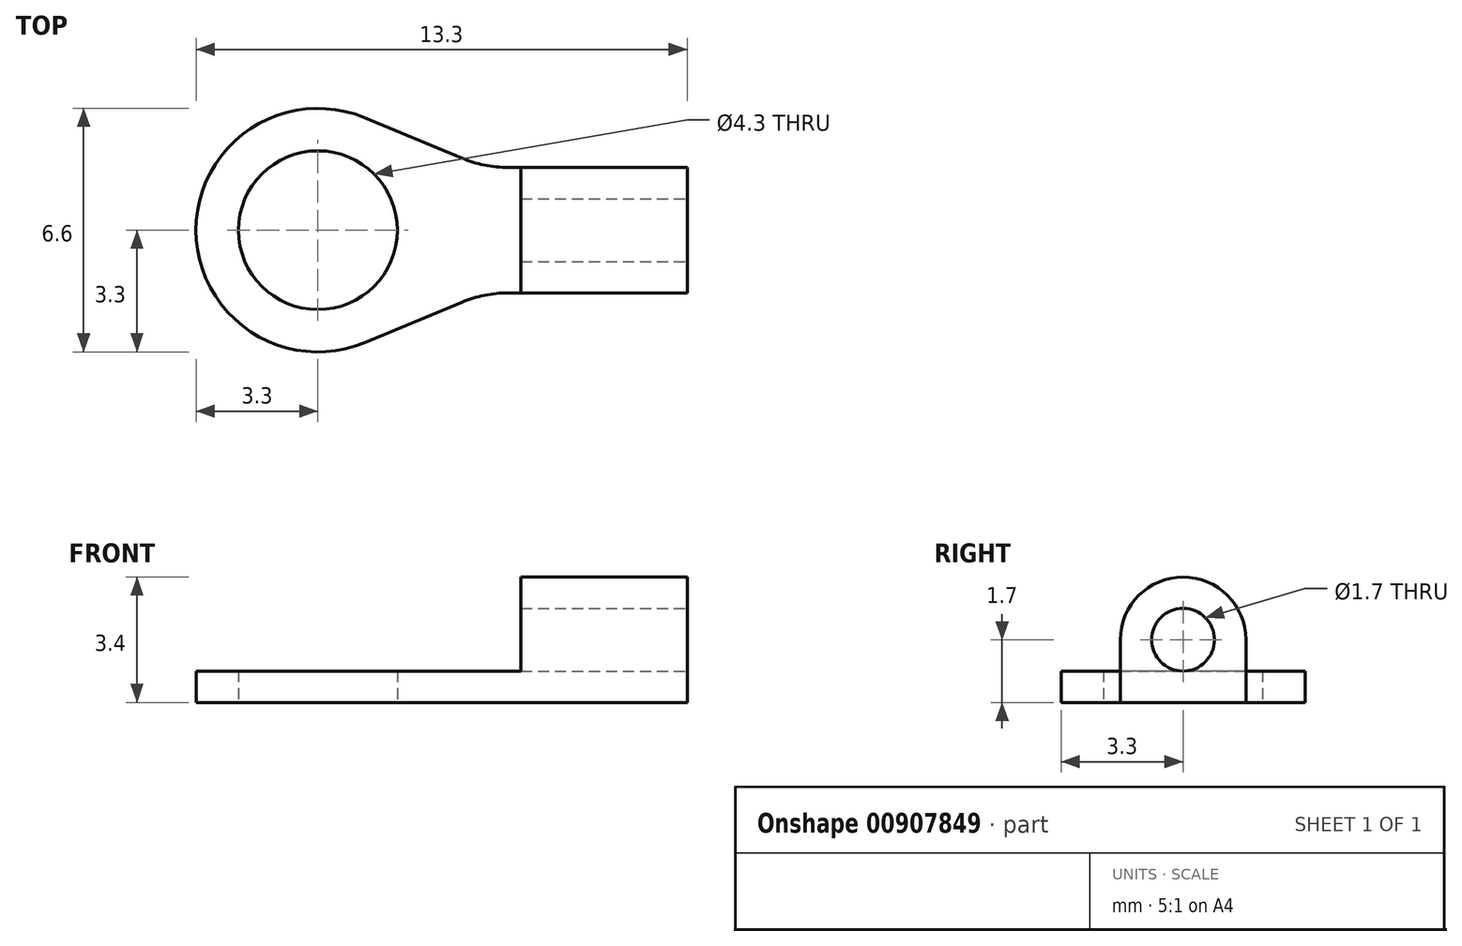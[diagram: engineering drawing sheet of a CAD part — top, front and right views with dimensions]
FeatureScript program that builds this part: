
annotation { "Feature Type Name" : "Feature", "Feature Type Description" : "" }
export const myFeature = defineFeature(function(context is Context, id is Id, definition is map)
    precondition{}
    {
        {
            var Q0;
            Q0=qCreatedBy(makeId("Top.planeOp"),FACE);
            var sketch = newSketch(context, id + "F0", { "sketchPlane" : qUnion([Q0])});
            skLineSegment(sketch, "E0.left", {"start": v(0, 3.3) * mm, "end": v(0, 3.3) * mm});
            skLineSegment(sketch, "E0.right", {"start": v(13.3, 1.6) * mm, "end": v(13.3, 5) * mm});
            skPoint(sketch, "E1.visualSharp", {"position": v(0, 6.6) * mm});
            skArc(sketch, "E1.filletArc", {"start": v(3.3, 6.6) * mm, "mid": v(0.97, 5.63) * mm, "end": v(0, 3.3) * mm});
            skPoint(sketch, "E2.visualSharp", {"position": v(0, 0) * mm});
            skArc(sketch, "E2.filletArc", {"start": v(0, 3.3) * mm, "mid": v(0.97, 0.97) * mm, "end": v(3.3, 0) * mm});
            skLineSegment(sketch, "E3.bottom", {"start": v(13.3, 1.6) * mm, "end": v(8.46, 1.6) * mm});
            skLineSegment(sketch, "E3.top", {"start": v(13.3, 5) * mm, "end": v(8.46, 5) * mm});
            skPoint(sketch, "E3.middle", {"position": v(13.3, 3.3) * mm});
            skArc(sketch, "E4", {"start": v(4.57, 6.35) * mm, "mid": v(0, 3.3) * mm, "end": v(4.57, 0.25) * mm});
            skCircle(sketch, "E5", {"center": v(3.3, 3.3) * mm, "radius": 2.15 * mm});
            skLineSegment(sketch, "E6", {"start": v(7.2, 5.25) * mm, "end": v(4.57, 6.35) * mm});
            skLineSegment(sketch, "E7", {"start": v(7.2, 1.35) * mm, "end": v(4.57, 0.25) * mm});
            skPoint(sketch, "E3.left.end.orphan", {"position": v(17.8, 5) * mm});
            skPoint(sketch, "E8.orphan", {"position": v(17.8, 1.6) * mm});
            skPoint(sketch, "E0.top.end.orphan", {"position": v(13.3, 6.6) * mm});
            skPoint(sketch, "E0.bottom.end.orphan", {"position": v(13.3, 0) * mm});
            skPoint(sketch, "E3.right.end.orphan", {"position": v(8.8, 5) * mm});
            skPoint(sketch, "E3.right.start.orphan", {"position": v(8.8, 1.6) * mm});
            skPoint(sketch, "E9.visualSharp", {"position": v(7.8, 5) * mm});
            skArc(sketch, "E9.filletArc", {"start": v(7.2, 5.25) * mm, "mid": v(7.81, 5.06) * mm, "end": v(8.46, 5) * mm});
            skPoint(sketch, "E10.visualSharp", {"position": v(7.8, 1.6) * mm});
            skArc(sketch, "E10.filletArc", {"start": v(8.46, 1.6) * mm, "mid": v(7.81, 1.54) * mm, "end": v(7.2, 1.35) * mm});
            skSolve(sketch);
        }
        {
            var Q0;
            Q0=makeQuery(id+"F0.imprint","IMPRINT",FACE,{"disambiguationData":[TD([[makeQuery(id+"F0.imprint","IMPRINT",EDGE,{"derivedFrom":sQuery(id+"F0.wireOp",EDGE,"E0.right")}),1.0]])]});
            extrude(context, id + "F1", {"entities" : qUnion([Q0]), "depth" : 0.85 * mm, "offsetDistance" : 25 * mm});
        }
        {
            var Q0;
            Q0=makeQuery(id+"F1.opExtrude","CAP_FACE",FACE,{"disambiguationData":[OSD([sQuery(id+"F0.wireOp",EDGE,"E0.right"),sQuery(id+"F0.wireOp",EDGE,"E3.bottom"),sQuery(id+"F0.wireOp",EDGE,"E3.top"),sQuery(id+"F0.wireOp",EDGE,"E4"),sQuery(id+"F0.wireOp",EDGE,"E5"),sQuery(id+"F0.wireOp",EDGE,"E6"),sQuery(id+"F0.wireOp",EDGE,"E7"),sQuery(id+"F0.wireOp",EDGE,"E9.filletArc"),sQuery(id+"F0.wireOp",EDGE,"E10.filletArc")])],"isStart":false});
            var sketch = newSketch(context, id + "F2", { "sketchPlane" : qUnion([Q0])});
            skLineSegment(sketch, "E11.bottom", {"start": v(13.3, 5) * mm, "end": v(8.8, 5) * mm});
            skLineSegment(sketch, "E11.top", {"start": v(13.3, 1.6) * mm, "end": v(8.8, 1.6) * mm});
            skLineSegment(sketch, "E11.left", {"start": v(13.3, 5) * mm, "end": v(13.3, 1.6) * mm});
            skLineSegment(sketch, "E11.right", {"start": v(8.8, 5) * mm, "end": v(8.8, 1.6) * mm});
            skSolve(sketch);
        }
        {
            var Q0;
            Q0 = qSketchRegion(id + "F2", true);
            extrude(context, id + "F3", {"entities" : qUnion([Q0]), "operationType" : NewBodyOperationType.ADD, "depth" : 2.55 * mm, "offsetDistance" : 25 * mm});
        }
        {
            var Q0;
            Q0=makeQuery(id+"F3.opExtrude","CAP_EDGE",EDGE,{"disambiguationData":[OSD([sQuery(id+"F2.wireOp",EDGE,"E11.bottom")])],"isStart":false});
            var Q1;
            Q1=makeQuery(id+"F3.opExtrude","CAP_EDGE",EDGE,{"disambiguationData":[OSD([sQuery(id+"F2.wireOp",EDGE,"E11.top")])],"isStart":false});
            fillet(context, id + "F4", {"entities" : qUnion([Q0, Q1]), "radius" : 1.7 * mm, "tangentPropagation" : true, "allowEdgeOverflow" : false});
        }
        {
            var Q0;
            Q0=makeQuery(id+"F3.boolean.opBoolean","MERGE",FACE,{"derivedFrom":[makeQuery(id+"F1.opExtrude","SWEPT_FACE",FACE,{"disambiguationData":[OSD([sQuery(id+"F0.wireOp",EDGE,"E0.right")])]}),makeQuery(id+"F3.opExtrude","SWEPT_FACE",FACE,{"disambiguationData":[OSD([sQuery(id+"F2.wireOp",EDGE,"E11.left")])]})]});
            var sketch = newSketch(context, id + "F5", { "sketchPlane" : qUnion([Q0])});
            skCircle(sketch, "E12", {"center": v(3.3, 1.7) * mm, "radius": 0.85 * mm});
            skSolve(sketch);
        }
        {
            var Q0;
            Q0=makeQuery(id+"F5.imprint","IMPRINT",FACE,{"disambiguationData":[TD([[makeQuery(id+"F5.imprint","IMPRINT",EDGE,{"derivedFrom":sQuery(id+"F5.wireOp",EDGE,"E12")}),1.0]])]});
            extrude(context, id + "F6", {"entities" : qUnion([Q0]), "operationType" : NewBodyOperationType.REMOVE, "oppositeDirection" : true, "depth" : 25 * mm, "offsetDistance" : 25 * mm});
        }
    });
